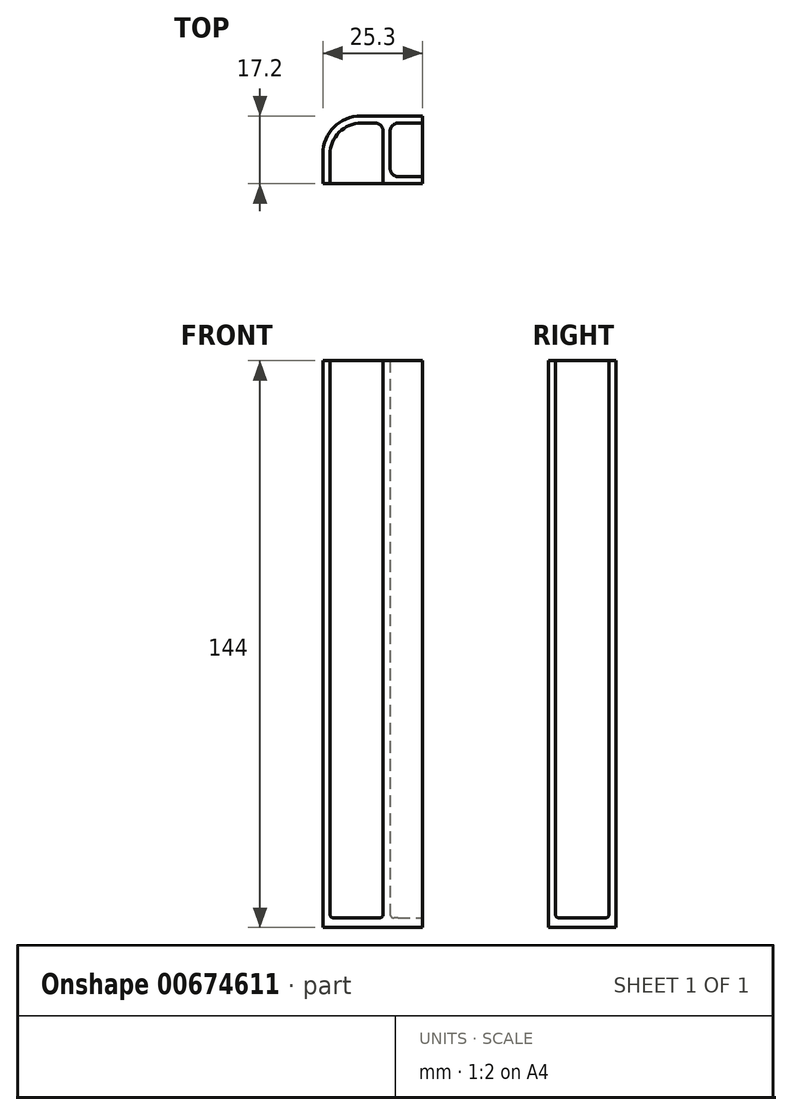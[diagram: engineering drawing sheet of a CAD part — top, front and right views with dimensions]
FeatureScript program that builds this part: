
annotation { "Feature Type Name" : "Feature", "Feature Type Description" : "" }
export const myFeature = defineFeature(function(context is Context, id is Id, definition is map)
    precondition{}
    {
        {
            var Q0;
            Q0=qCreatedBy(makeId("Top.planeOp"),FACE);
            var sketch = newSketch(context, id + "F0", { "sketchPlane" : qUnion([Q0])});
            skLineSegment(sketch, "E0.bottom", {"start": v(0, 0) * mm, "end": v(-13.5, 0) * mm});
            skLineSegment(sketch, "E0.top", {"start": v(0, -17.2) * mm, "end": v(-13.5, -17.2) * mm});
            skLineSegment(sketch, "E0.left", {"start": v(0, 0) * mm, "end": v(0, -17.2) * mm});
            skLineSegment(sketch, "E0.right", {"start": v(-13.5, 0) * mm, "end": v(-13.5, -17.2) * mm});
            skLineSegment(sketch, "E1", {"start": v(-13.5, -17.2) * mm, "end": v(-15.3, -17.2) * mm});
            skLineSegment(sketch, "E2", {"start": v(-15.3, -17.2) * mm, "end": v(-15.3, 0) * mm});
            skLineSegment(sketch, "E3", {"start": v(-15.3, 0) * mm, "end": v(-13.5, 0) * mm});
            skLineSegment(sketch, "E4", {"start": v(-13.5, -1.8) * mm, "end": v(0, -1.8) * mm});
            skLineSegment(sketch, "E5", {"start": v(0, 0) * mm, "end": v(10, 0) * mm});
            skLineSegment(sketch, "E6", {"start": v(10, 0) * mm, "end": v(10, -17.2) * mm});
            skLineSegment(sketch, "E7", {"start": v(0, -17.2) * mm, "end": v(10, -17.2) * mm});
            skLineSegment(sketch, "E8", {"start": v(0, -1.8) * mm, "end": v(10, -1.8) * mm});
            skLineSegment(sketch, "E9", {"start": v(1.8, -1.8) * mm, "end": v(1.8, -17.2) * mm});
            skLineSegment(sketch, "E10", {"start": v(1.8, -15.4) * mm, "end": v(10, -15.4) * mm});
            skSolve(sketch);
        }
        {
            var Q0;
            {var subQ0=sQuery(id+"F0.wireOp",EDGE,"E1");Q0=makeQuery(id+"F0.imprint","IMPRINT",FACE,{"disambiguationData":[TD([[makeQuery(id+"F0.imprint","IMPRINT",EDGE,{"derivedFrom":subQ0}),-1.0]])]});}
            var Q1;
            {var subQ0=sQuery(id+"F0.wireOp",EDGE,"E0.bottom");Q1=makeQuery(id+"F0.imprint","IMPRINT",FACE,{"disambiguationData":[TD([[makeQuery(id+"F0.imprint","IMPRINT",EDGE,{"derivedFrom":subQ0}),1.0]])]});}
            var Q2;
            {var subQ0=sQuery(id+"F0.wireOp",EDGE,"E0.top");Q2=makeQuery(id+"F0.imprint","IMPRINT",FACE,{"disambiguationData":[TD([[makeQuery(id+"F0.imprint","IMPRINT",EDGE,{"derivedFrom":subQ0}),-1.0]])]});}
            var Q3;
            {var subQ0=sQuery(id+"F0.wireOp",EDGE,"E8");var subQ3=sQuery(id+"F0.wireOp",EDGE,"E9");var subQ4=makeQuery(id+"F0.imprint","INTERSECT",VERTEX,{"derivedFrom":[subQ0,subQ3]});Q3=makeQuery(id+"F0.imprint","IMPRINT",FACE,{"disambiguationData":[TD([[makeQuery(id+"F0.imprint","IMPRINT",EDGE,{"disambiguationData":[TD([[subQ4,-1.0]])],"derivedFrom":subQ3}),-1.0]])]});}
            var Q4;
            {var subQ3=sQuery(id+"F0.wireOp",EDGE,"E10");Q4=makeQuery(id+"F0.imprint","IMPRINT",FACE,{"disambiguationData":[TD([[makeQuery(id+"F0.imprint","IMPRINT",EDGE,{"derivedFrom":subQ3}),-1.0]])]});}
            var Q5;
            {var subQ3=sQuery(id+"F0.wireOp",EDGE,"E10");Q5=makeQuery(id+"F0.imprint","IMPRINT",FACE,{"disambiguationData":[TD([[makeQuery(id+"F0.imprint","IMPRINT",EDGE,{"derivedFrom":subQ3}),1.0]])]});}
            var Q6;
            {var subQ5=sQuery(id+"F0.wireOp",EDGE,"E5");Q6=makeQuery(id+"F0.imprint","IMPRINT",FACE,{"disambiguationData":[TD([[makeQuery(id+"F0.imprint","IMPRINT",EDGE,{"derivedFrom":subQ5}),-1.0]])]});}
            extrude(context, id + "F1", {"entities" : qUnion([Q0, Q1, Q2, Q3, Q4, Q5, Q6]), "oppositeDirection" : true, "depth" : 2.4 * mm, "offsetDistance" : 25 * mm});
        }
        {
            var Q0;
            {var subQ0=sQuery(id+"F0.wireOp",EDGE,"E1");Q0=makeQuery(id+"F0.imprint","IMPRINT",FACE,{"disambiguationData":[TD([[makeQuery(id+"F0.imprint","IMPRINT",EDGE,{"derivedFrom":subQ0}),-1.0]])]});}
            var Q1;
            {var subQ0=sQuery(id+"F0.wireOp",EDGE,"E8");var subQ3=sQuery(id+"F0.wireOp",EDGE,"E9");var subQ4=makeQuery(id+"F0.imprint","INTERSECT",VERTEX,{"derivedFrom":[subQ0,subQ3]});Q1=makeQuery(id+"F0.imprint","IMPRINT",FACE,{"disambiguationData":[TD([[makeQuery(id+"F0.imprint","IMPRINT",EDGE,{"disambiguationData":[TD([[subQ4,-1.0]])],"derivedFrom":subQ3}),-1.0]])]});}
            var Q2;
            {var subQ0=sQuery(id+"F0.wireOp",EDGE,"E0.bottom");Q2=makeQuery(id+"F0.imprint","IMPRINT",FACE,{"disambiguationData":[TD([[makeQuery(id+"F0.imprint","IMPRINT",EDGE,{"derivedFrom":subQ0}),1.0]])]});}
            var Q3;
            {var subQ5=sQuery(id+"F0.wireOp",EDGE,"E5");Q3=makeQuery(id+"F0.imprint","IMPRINT",FACE,{"disambiguationData":[TD([[makeQuery(id+"F0.imprint","IMPRINT",EDGE,{"derivedFrom":subQ5}),-1.0]])]});}
            var Q4;
            {var subQ3=sQuery(id+"F0.wireOp",EDGE,"E10");Q4=makeQuery(id+"F0.imprint","IMPRINT",FACE,{"disambiguationData":[TD([[makeQuery(id+"F0.imprint","IMPRINT",EDGE,{"derivedFrom":subQ3}),-1.0]])]});}
            extrude(context, id + "F2", {"entities" : qUnion([Q0, Q1, Q2, Q3, Q4]), "operationType" : NewBodyOperationType.ADD, "depth" : 141.6 * mm, "offsetDistance" : 25 * mm});
        }
        {
            var Q0;
            Q0=makeQuery(id+"F2.opExtrude","SWEPT_EDGE",EDGE,{"disambiguationData":[OSD([sQuery(id+"F0.wireOp",EDGE,"E0.right"),sQuery(id+"F0.wireOp",EDGE,"E4")])]});
            fillet(context, id + "F3", {"entities" : qUnion([Q0]), "radius" : 8 * mm, "tangentPropagation" : true, "allowEdgeOverflow" : false});
        }
        {
            var Q0;
            {var subQ0=sQuery(id+"F0.wireOp",EDGE,"E3");var subQ1=sQuery(id+"F0.wireOp",EDGE,"E2");Q0=makeQuery(id+"F2.boolean.opBoolean","MERGE",EDGE,{"derivedFrom":[makeQuery(id+"F1.opExtrude","SWEPT_EDGE",EDGE,{"disambiguationData":[OSD([subQ1,subQ0])]}),makeQuery(id+"F2.opExtrude","SWEPT_EDGE",EDGE,{"disambiguationData":[OSD([subQ1,subQ0])]})]});}
            fillet(context, id + "F4", {"entities" : qUnion([Q0]), "radius" : 9.6 * mm, "tangentPropagation" : true, "allowEdgeOverflow" : false});
        }
        {
            var Q0;
            Q0=makeQuery(id+"F2.opExtrude","SWEPT_EDGE",EDGE,{"disambiguationData":[OSD([sQuery(id+"F0.wireOp",EDGE,"E0.left"),sQuery(id+"F0.wireOp",EDGE,"E4"),sQuery(id+"F0.wireOp",EDGE,"E8")])]});
            var Q1;
            Q1=makeQuery(id+"F2.opExtrude","SWEPT_EDGE",EDGE,{"disambiguationData":[OSD([sQuery(id+"F0.wireOp",EDGE,"E8"),sQuery(id+"F0.wireOp",EDGE,"E9")])]});
            var Q2;
            Q2=makeQuery(id+"F2.opExtrude","SWEPT_EDGE",EDGE,{"disambiguationData":[OSD([sQuery(id+"F0.wireOp",EDGE,"E9"),sQuery(id+"F0.wireOp",EDGE,"E10")])]});
            fillet(context, id + "F5", {"entities" : qUnion([Q0, Q1, Q2]), "radius" : 2 * mm, "tangentPropagation" : true, "allowEdgeOverflow" : false});
        }
        {
            var Q0;
            Q0=makeQuery(id+"F2.opExtrude","CAP_EDGE",EDGE,{"disambiguationData":[OSD([sQuery(id+"F0.wireOp",EDGE,"E10")])],"isStart":true});
            var Q1;
            {var subQ1=sQuery(id+"F0.wireOp",EDGE,"E6");var subQ2=sQuery(id+"F0.wireOp",EDGE,"E5");var subQ3=sQuery(id+"F0.wireOp",EDGE,"E7");var subQ4=sQuery(id+"F0.wireOp",EDGE,"E10");var subQ5=sQuery(id+"F0.wireOp",EDGE,"E9");Q1=makeQuery(id+"F5.opFillet","BLEND_EDGE",EDGE,{"blendedFrom":[makeQuery(id+"F2.opExtrude","SWEPT_EDGE",EDGE,{"disambiguationData":[OSD([subQ5,subQ4])]}),makeQuery(id+"F2.boolean.opBoolean","SPLIT",FACE,{"disambiguationData":[TD([makeQuery(id+"F1.opExtrude","SWEPT_FACE",FACE,{"disambiguationData":[OSD([subQ1])]})])],"derivedFrom":makeQuery(id+"F1.opExtrude","CAP_FACE",FACE,{"disambiguationData":[OSD([sQuery(id+"F0.wireOp",EDGE,"E0.bottom"),sQuery(id+"F0.wireOp",EDGE,"E0.top"),sQuery(id+"F0.wireOp",EDGE,"E1"),sQuery(id+"F0.wireOp",EDGE,"E2"),sQuery(id+"F0.wireOp",EDGE,"E3"),subQ2,subQ1,subQ3])],"isStart":true})})],"blendedInto":[makeQuery(id+"F2.boolean.opBoolean","SPLIT",FACE,{"disambiguationData":[TD([makeQuery(id+"F1.opExtrude","SWEPT_FACE",FACE,{"disambiguationData":[OSD([subQ1])]})])],"derivedFrom":makeQuery(id+"F1.opExtrude","CAP_FACE",FACE,{"disambiguationData":[OSD([sQuery(id+"F0.wireOp",EDGE,"E0.bottom"),sQuery(id+"F0.wireOp",EDGE,"E0.top"),sQuery(id+"F0.wireOp",EDGE,"E1"),sQuery(id+"F0.wireOp",EDGE,"E2"),sQuery(id+"F0.wireOp",EDGE,"E3"),subQ2,subQ1,subQ3])],"isStart":true})})]});}
            var Q2;
            Q2=makeQuery(id+"F2.opExtrude","CAP_EDGE",EDGE,{"disambiguationData":[OSD([sQuery(id+"F0.wireOp",EDGE,"E9")])],"isStart":true});
            var Q3;
            {var subQ0=sQuery(id+"F0.wireOp",EDGE,"E8");var subQ1=sQuery(id+"F0.wireOp",EDGE,"E6");var subQ2=sQuery(id+"F0.wireOp",EDGE,"E5");var subQ3=sQuery(id+"F0.wireOp",EDGE,"E7");var subQ5=sQuery(id+"F0.wireOp",EDGE,"E9");Q3=makeQuery(id+"F5.opFillet","BLEND_EDGE",EDGE,{"blendedFrom":[makeQuery(id+"F2.opExtrude","SWEPT_EDGE",EDGE,{"disambiguationData":[OSD([subQ0,subQ5])]}),makeQuery(id+"F2.boolean.opBoolean","SPLIT",FACE,{"disambiguationData":[TD([makeQuery(id+"F1.opExtrude","SWEPT_FACE",FACE,{"disambiguationData":[OSD([subQ1])]})])],"derivedFrom":makeQuery(id+"F1.opExtrude","CAP_FACE",FACE,{"disambiguationData":[OSD([sQuery(id+"F0.wireOp",EDGE,"E0.bottom"),sQuery(id+"F0.wireOp",EDGE,"E0.top"),sQuery(id+"F0.wireOp",EDGE,"E1"),sQuery(id+"F0.wireOp",EDGE,"E2"),sQuery(id+"F0.wireOp",EDGE,"E3"),subQ2,subQ1,subQ3])],"isStart":true})})],"blendedInto":[makeQuery(id+"F2.boolean.opBoolean","SPLIT",FACE,{"disambiguationData":[TD([makeQuery(id+"F1.opExtrude","SWEPT_FACE",FACE,{"disambiguationData":[OSD([subQ1])]})])],"derivedFrom":makeQuery(id+"F1.opExtrude","CAP_FACE",FACE,{"disambiguationData":[OSD([sQuery(id+"F0.wireOp",EDGE,"E0.bottom"),sQuery(id+"F0.wireOp",EDGE,"E0.top"),sQuery(id+"F0.wireOp",EDGE,"E1"),sQuery(id+"F0.wireOp",EDGE,"E2"),sQuery(id+"F0.wireOp",EDGE,"E3"),subQ2,subQ1,subQ3])],"isStart":true})})]});}
            var Q4;
            Q4=makeQuery(id+"F2.opExtrude","CAP_EDGE",EDGE,{"disambiguationData":[OSD([sQuery(id+"F0.wireOp",EDGE,"E8")])],"isStart":true});
            var Q5;
            Q5=makeQuery(id+"F2.opExtrude","CAP_EDGE",EDGE,{"disambiguationData":[OSD([sQuery(id+"F0.wireOp",EDGE,"E0.left")])],"isStart":true});
            var Q6;
            {var subQ0=sQuery(id+"F0.wireOp",EDGE,"E1");var subQ1=sQuery(id+"F0.wireOp",EDGE,"E0.left");var subQ2=sQuery(id+"F0.wireOp",EDGE,"E7");var subQ3=sQuery(id+"F0.wireOp",EDGE,"E0.top");var subQ4=sQuery(id+"F0.wireOp",EDGE,"E4");Q6=makeQuery(id+"F5.opFillet","BLEND_EDGE",EDGE,{"blendedFrom":[makeQuery(id+"F2.opExtrude","SWEPT_EDGE",EDGE,{"disambiguationData":[OSD([subQ1,subQ4,sQuery(id+"F0.wireOp",EDGE,"E8")])]}),makeQuery(id+"F2.boolean.opBoolean","SPLIT",FACE,{"disambiguationData":[TD([makeQuery(id+"F2.opExtrude","SWEPT_FACE",FACE,{"disambiguationData":[OSD([subQ1])]})])],"derivedFrom":makeQuery(id+"F1.opExtrude","CAP_FACE",FACE,{"disambiguationData":[OSD([sQuery(id+"F0.wireOp",EDGE,"E0.bottom"),subQ3,subQ0,sQuery(id+"F0.wireOp",EDGE,"E2"),sQuery(id+"F0.wireOp",EDGE,"E3"),sQuery(id+"F0.wireOp",EDGE,"E5"),sQuery(id+"F0.wireOp",EDGE,"E6"),subQ2])],"isStart":true})})],"blendedInto":[makeQuery(id+"F2.boolean.opBoolean","SPLIT",FACE,{"disambiguationData":[TD([makeQuery(id+"F2.opExtrude","SWEPT_FACE",FACE,{"disambiguationData":[OSD([subQ1])]})])],"derivedFrom":makeQuery(id+"F1.opExtrude","CAP_FACE",FACE,{"disambiguationData":[OSD([sQuery(id+"F0.wireOp",EDGE,"E0.bottom"),subQ3,subQ0,sQuery(id+"F0.wireOp",EDGE,"E2"),sQuery(id+"F0.wireOp",EDGE,"E3"),sQuery(id+"F0.wireOp",EDGE,"E5"),sQuery(id+"F0.wireOp",EDGE,"E6"),subQ2])],"isStart":true})})]});}
            var Q7;
            Q7=makeQuery(id+"F2.opExtrude","CAP_EDGE",EDGE,{"disambiguationData":[OSD([sQuery(id+"F0.wireOp",EDGE,"E4")])],"isStart":true});
            var Q8;
            {var subQ0=sQuery(id+"F0.wireOp",EDGE,"E1");var subQ1=sQuery(id+"F0.wireOp",EDGE,"E0.right");var subQ2=sQuery(id+"F0.wireOp",EDGE,"E7");var subQ3=sQuery(id+"F0.wireOp",EDGE,"E0.top");var subQ4=sQuery(id+"F0.wireOp",EDGE,"E4");Q8=makeQuery(id+"F3.opFillet","BLEND_EDGE",EDGE,{"blendedFrom":[makeQuery(id+"F2.opExtrude","SWEPT_EDGE",EDGE,{"disambiguationData":[OSD([subQ1,subQ4])]}),makeQuery(id+"F2.boolean.opBoolean","SPLIT",FACE,{"disambiguationData":[TD([makeQuery(id+"F2.opExtrude","SWEPT_FACE",FACE,{"disambiguationData":[OSD([sQuery(id+"F0.wireOp",EDGE,"E0.left")])]})])],"derivedFrom":makeQuery(id+"F1.opExtrude","CAP_FACE",FACE,{"disambiguationData":[OSD([sQuery(id+"F0.wireOp",EDGE,"E0.bottom"),subQ3,subQ0,sQuery(id+"F0.wireOp",EDGE,"E2"),sQuery(id+"F0.wireOp",EDGE,"E3"),sQuery(id+"F0.wireOp",EDGE,"E5"),sQuery(id+"F0.wireOp",EDGE,"E6"),subQ2])],"isStart":true})})],"blendedInto":[makeQuery(id+"F2.boolean.opBoolean","SPLIT",FACE,{"disambiguationData":[TD([makeQuery(id+"F2.opExtrude","SWEPT_FACE",FACE,{"disambiguationData":[OSD([sQuery(id+"F0.wireOp",EDGE,"E0.left")])]})])],"derivedFrom":makeQuery(id+"F1.opExtrude","CAP_FACE",FACE,{"disambiguationData":[OSD([sQuery(id+"F0.wireOp",EDGE,"E0.bottom"),subQ3,subQ0,sQuery(id+"F0.wireOp",EDGE,"E2"),sQuery(id+"F0.wireOp",EDGE,"E3"),sQuery(id+"F0.wireOp",EDGE,"E5"),sQuery(id+"F0.wireOp",EDGE,"E6"),subQ2])],"isStart":true})})]});}
            var Q9;
            Q9=makeQuery(id+"F2.opExtrude","CAP_EDGE",EDGE,{"disambiguationData":[OSD([sQuery(id+"F0.wireOp",EDGE,"E0.right")])],"isStart":true});
            fillet(context, id + "F6", {"entities" : qUnion([Q0, Q1, Q2, Q3, Q4, Q5, Q6, Q7, Q8, Q9]), "radius" : 1 * mm, "tangentPropagation" : true, "allowEdgeOverflow" : false});
        }
    });
